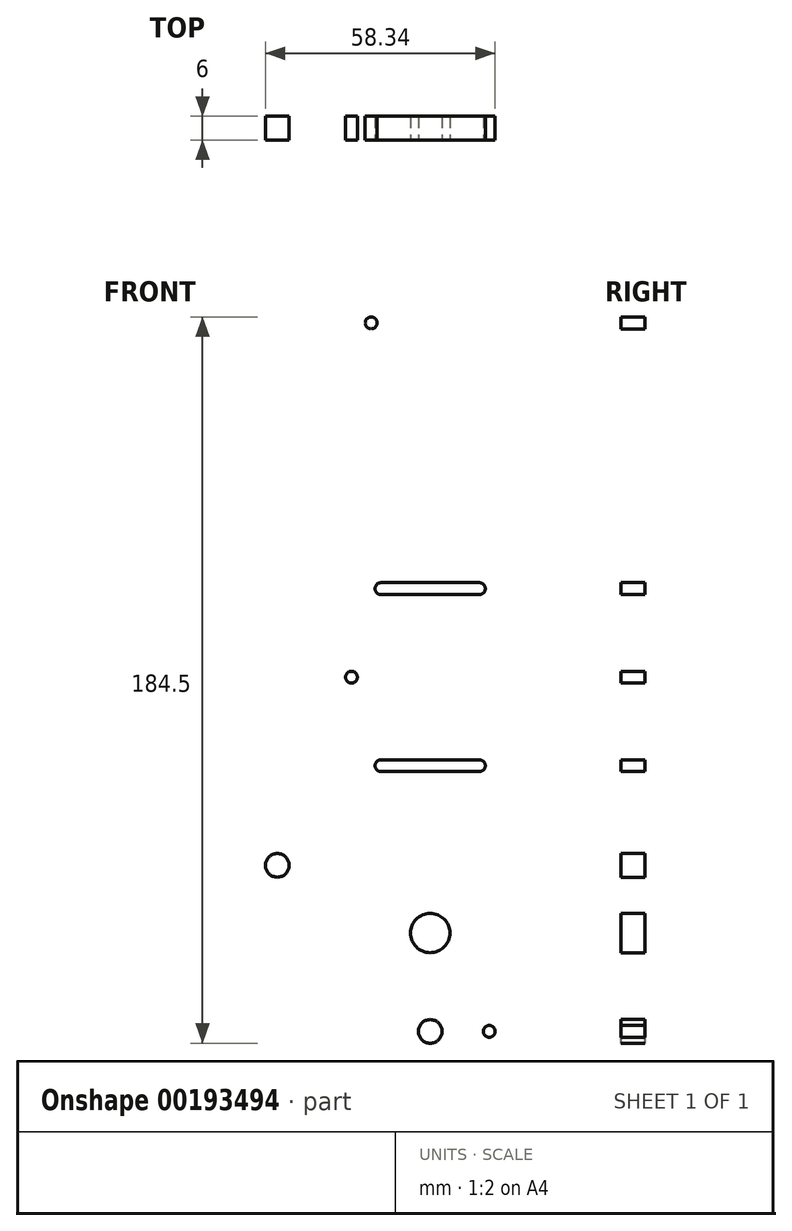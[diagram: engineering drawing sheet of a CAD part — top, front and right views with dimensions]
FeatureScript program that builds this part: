
annotation { "Feature Type Name" : "Feature", "Feature Type Description" : "" }
export const myFeature = defineFeature(function(context is Context, id is Id, definition is map)
    precondition{}
    {
        {
            var Q0;
            Q0=qCreatedBy(makeId("Front.planeOp"),FACE);
            var sketch = newSketch(context, id + "F0", { "sketchPlane" : qUnion([Q0])});
            skLineSegment(sketch, "E0.bottom", {"start": v(-75, 100) * mm, "end": v(75, 100) * mm});
            skLineSegment(sketch, "E0.top", {"start": v(-75, -100) * mm, "end": v(75, -100) * mm});
            skLineSegment(sketch, "E0.left", {"start": v(-75, 100) * mm, "end": v(-75, -100) * mm});
            skLineSegment(sketch, "E0.right", {"start": v(75, 100) * mm, "end": v(75, -100) * mm});
            skPoint(sketch, "E0.middle", {"position": v(0, 0) * mm});
            skSolve(sketch);
        }
        {
            var Q0;
            Q0=makeQuery(id+"F0.imprint","IMPRINT",FACE,{"disambiguationData":[TD([[makeQuery(id+"F0.imprint","IMPRINT",EDGE,{"derivedFrom":sQuery(id+"F0.wireOp",EDGE,"E0.bottom")}),-1.0]])]});
            extrude(context, id + "F1", {"entities" : qUnion([Q0]), "depth" : 3 * mm, "hasSecondDirection" : true, "secondDirectionOppositeDirection" : true, "secondDirectionDepth" : 3 * mm});
        }
        {
            var Q0;
            Q0=makeQuery(id+"F1.opExtrude","SWEPT_EDGE",EDGE,{"disambiguationData":[OSD([sQuery(id+"F0.wireOp",EDGE,"E0.top"),sQuery(id+"F0.wireOp",EDGE,"E0.left")])]});
            var Q1;
            Q1=makeQuery(id+"F1.opExtrude","SWEPT_EDGE",EDGE,{"disambiguationData":[OSD([sQuery(id+"F0.wireOp",EDGE,"E0.top"),sQuery(id+"F0.wireOp",EDGE,"E0.right")])]});
            var Q2;
            Q2=makeQuery(id+"F1.opExtrude","SWEPT_EDGE",EDGE,{"disambiguationData":[OSD([sQuery(id+"F0.wireOp",EDGE,"E0.bottom"),sQuery(id+"F0.wireOp",EDGE,"E0.right")])]});
            var Q3;
            Q3=makeQuery(id+"F1.opExtrude","SWEPT_EDGE",EDGE,{"disambiguationData":[OSD([sQuery(id+"F0.wireOp",EDGE,"E0.bottom"),sQuery(id+"F0.wireOp",EDGE,"E0.left")])]});
            fillet(context, id + "F2", {"entities" : qUnion([Q0, Q1, Q2, Q3]), "radius" : 10 * mm, "tangentPropagation" : true, "allowEdgeOverflow" : false});
        }
        {
            var Q0;
            Q0=makeQuery(id+"F1.opExtrude","CAP_FACE",FACE,{"disambiguationData":[OSD([sQuery(id+"F0.wireOp",EDGE,"E0.bottom"),sQuery(id+"F0.wireOp",EDGE,"E0.top"),sQuery(id+"F0.wireOp",EDGE,"E0.left"),sQuery(id+"F0.wireOp",EDGE,"E0.right")])],"isStart":false});
            var sketch = newSketch(context, id + "F3", { "sketchPlane" : qUnion([Q0])});
            skPoint(sketch, "E1.middle", {"position": v(0, 0) * mm});
            skPoint(sketch, "E2", {"position": v(62.5, -80) * mm});
            skPoint(sketch, "E3", {"position": v(62.5, -50) * mm});
            skPoint(sketch, "E4.MirrorP", {"position": v(-62.5, -50) * mm});
            skPoint(sketch, "E5.MirrorP", {"position": v(-62.5, -80) * mm});
            skPoint(sketch, "E6.MirrorP", {"position": v(62.5, 50) * mm});
            skPoint(sketch, "E7.MirrorP", {"position": v(62.5, 80) * mm});
            skPoint(sketch, "E8.MirrorP", {"position": v(-62.5, 50) * mm});
            skPoint(sketch, "E9.MirrorP", {"position": v(-62.5, 80) * mm});
            skSolve(sketch);
        }
        {
            var Q0;
            Q0=sQuery(id+"F3.wireOp",VERTEX,"E2");
            var Q1;
            Q1=sQuery(id+"F3.wireOp",VERTEX,"E3");
            var Q2;
            Q2=sQuery(id+"F3.wireOp",VERTEX,"E6.MirrorP");
            var Q3;
            Q3=sQuery(id+"F3.wireOp",VERTEX,"E7.MirrorP");
            var Q4;
            Q4=sQuery(id+"F3.wireOp",VERTEX,"E9.MirrorP");
            var Q5;
            Q5=sQuery(id+"F3.wireOp",VERTEX,"E8.MirrorP");
            var Q6;
            Q6=sQuery(id+"F3.wireOp",VERTEX,"E4.MirrorP");
            var Q7;
            Q7=sQuery(id+"F3.wireOp",VERTEX,"E5.MirrorP");
            var Q8;
            Q8=makeQuery(id+"F1.opExtrude","SWEPT_BODY",BODY,{"disambiguationData":[OSD([sQuery(id+"F0.wireOp",EDGE,"E0.bottom"),sQuery(id+"F0.wireOp",EDGE,"E0.top"),sQuery(id+"F0.wireOp",EDGE,"E0.left"),sQuery(id+"F0.wireOp",EDGE,"E0.right")])]});
            hole(context, id + "F4", {"style" : HoleStyle.SIMPLE, "endStyle" : HoleEndStyle.BLIND, "holeDiameter" : 3 * mm, "holeDepth" : 12 * mm, "locations" : qUnion([Q0, Q1, Q2, Q3, Q4, Q5, Q6, Q7]), "scope" : qUnion([Q8])});
        }
        {
            var Q0;
            Q0=makeQuery(id+"F1.opExtrude","CAP_FACE",FACE,{"disambiguationData":[OSD([sQuery(id+"F0.wireOp",EDGE,"E0.bottom"),sQuery(id+"F0.wireOp",EDGE,"E0.top"),sQuery(id+"F0.wireOp",EDGE,"E0.left"),sQuery(id+"F0.wireOp",EDGE,"E0.right")])],"isStart":false});
            var sketch = newSketch(context, id + "F5", { "sketchPlane" : qUnion([Q0])});
            skPoint(sketch, "E10.middle", {"position": v(0, 0) * mm});
            skLineSegment(sketch, "E11.bottom", {"start": v(48, 10) * mm, "end": v(32, 10) * mm});
            skLineSegment(sketch, "E11.top", {"start": v(48, -10) * mm, "end": v(32, -10) * mm});
            skLineSegment(sketch, "E11.left", {"start": v(48, 10) * mm, "end": v(48, -10) * mm});
            skLineSegment(sketch, "E11.right", {"start": v(32, 10) * mm, "end": v(32, -10) * mm});
            skPoint(sketch, "E11.middle", {"position": v(40, 0) * mm});
            skPoint(sketch, "E12.MirrorP", {"position": v(-40, 0) * mm});
            skLineSegment(sketch, "E13.MirrorCS", {"start": v(-48, 10) * mm, "end": v(-32, 10) * mm});
            skLineSegment(sketch, "E14.MirrorCS", {"start": v(-32, 10) * mm, "end": v(-32, -10) * mm});
            skLineSegment(sketch, "E15.MirrorCS", {"start": v(-48, -10) * mm, "end": v(-32, -10) * mm});
            skLineSegment(sketch, "E16.MirrorCS", {"start": v(-48, 10) * mm, "end": v(-48, -10) * mm});
            skArc(sketch, "E17.0.startCap", {"start": v(12.5, 24) * mm, "mid": v(14, 22.5) * mm, "end": v(12.5, 21) * mm});
            skArc(sketch, "E17.0.endCap", {"start": v(-12.5, 21) * mm, "mid": v(-14, 22.5) * mm, "end": v(-12.5, 24) * mm});
            skLineSegment(sketch, "E17.0.left", {"start": v(12.5, 21) * mm, "end": v(-12.5, 21) * mm});
            skLineSegment(sketch, "E17.0.right", {"start": v(12.5, 24) * mm, "end": v(-12.5, 24) * mm});
            skArc(sketch, "E18.0.startCap", {"start": v(12.5, -21) * mm, "mid": v(14, -22.5) * mm, "end": v(12.5, -24) * mm});
            skArc(sketch, "E18.0.endCap", {"start": v(-12.5, -24) * mm, "mid": v(-14, -22.5) * mm, "end": v(-12.5, -21) * mm});
            skLineSegment(sketch, "E18.0.left", {"start": v(12.5, -24) * mm, "end": v(-12.5, -24) * mm});
            skLineSegment(sketch, "E18.0.right", {"start": v(12.5, -21) * mm, "end": v(-12.5, -21) * mm});
            skCircle(sketch, "E19", {"center": v(0, 65) * mm, "radius": 5 * mm});
            skCircle(sketch, "E20.MirrorC", {"center": v(0, -65) * mm, "radius": 5 * mm});
            skPoint(sketch, "E21.endSnap0", {"position": v(0, 100) * mm});
            skCircle(sketch, "E22", {"center": v(0, 90) * mm, "radius": 3 * mm});
            skCircle(sketch, "E23", {"center": v(15, 90) * mm, "radius": 1.5 * mm});
            skCircle(sketch, "E24.MirrorC", {"center": v(-15, 90) * mm, "radius": 1.5 * mm});
            skCircle(sketch, "E25.MirrorC", {"center": v(-15, -90) * mm, "radius": 1.5 * mm});
            skCircle(sketch, "E26.MirrorC", {"center": v(15, -90) * mm, "radius": 1.5 * mm});
            skCircle(sketch, "E27.MirrorC", {"center": v(0, -90) * mm, "radius": 3 * mm});
            skCircle(sketch, "E28", {"center": v(20, 0) * mm, "radius": 1.5 * mm});
            skCircle(sketch, "E29.MirrorC", {"center": v(-20, 0) * mm, "radius": 1.5 * mm});
            skCircle(sketch, "E30", {"center": v(38.84, -47.82) * mm, "radius": 3 * mm});
            skCircle(sketch, "E31.MirrorC", {"center": v(-38.84, -47.82) * mm, "radius": 3 * mm});
            skSolve(sketch);
        }
        {
            var Q0;
            Q0=makeQuery(id+"F5.imprint","IMPRINT",FACE,{"disambiguationData":[TD([[makeQuery(id+"F5.imprint","IMPRINT",EDGE,{"derivedFrom":sQuery(id+"F5.wireOp",EDGE,"E13.MirrorCS")}),-1.0]])]});
            var Q1;
            Q1=makeQuery(id+"F5.imprint","IMPRINT",FACE,{"disambiguationData":[TD([[makeQuery(id+"F5.imprint","IMPRINT",EDGE,{"derivedFrom":sQuery(id+"F5.wireOp",EDGE,"E17.0.startCap")}),-1.0]])]});
            var Q2;
            Q2=makeQuery(id+"F5.imprint","IMPRINT",FACE,{"disambiguationData":[TD([[makeQuery(id+"F5.imprint","IMPRINT",EDGE,{"derivedFrom":sQuery(id+"F5.wireOp",EDGE,"E18.0.startCap")}),-1.0]])]});
            var Q3;
            Q3=makeQuery(id+"F5.imprint","IMPRINT",FACE,{"disambiguationData":[TD([[makeQuery(id+"F5.imprint","IMPRINT",EDGE,{"derivedFrom":sQuery(id+"F5.wireOp",EDGE,"E11.bottom")}),1.0]])]});
            var Q4;
            Q4=makeQuery(id+"F5.imprint","IMPRINT",FACE,{"disambiguationData":[TD([[makeQuery(id+"F5.imprint","IMPRINT",EDGE,{"derivedFrom":sQuery(id+"F5.wireOp",EDGE,"E28")}),1.0]])]});
            var Q5;
            Q5=makeQuery(id+"F5.imprint","IMPRINT",FACE,{"disambiguationData":[TD([[makeQuery(id+"F5.imprint","IMPRINT",EDGE,{"derivedFrom":sQuery(id+"F5.wireOp",EDGE,"E20.MirrorC")}),-1.0]])]});
            var Q6;
            Q6=makeQuery(id+"F5.imprint","IMPRINT",FACE,{"disambiguationData":[TD([[makeQuery(id+"F5.imprint","IMPRINT",EDGE,{"derivedFrom":sQuery(id+"F5.wireOp",EDGE,"E31.MirrorC")}),-1.0]])]});
            var Q7;
            Q7=makeQuery(id+"F5.imprint","IMPRINT",FACE,{"disambiguationData":[TD([[makeQuery(id+"F5.imprint","IMPRINT",EDGE,{"derivedFrom":sQuery(id+"F5.wireOp",EDGE,"E30")}),1.0]])]});
            var Q8;
            Q8=makeQuery(id+"F5.imprint","IMPRINT",FACE,{"disambiguationData":[TD([[makeQuery(id+"F5.imprint","IMPRINT",EDGE,{"derivedFrom":sQuery(id+"F5.wireOp",EDGE,"E27.MirrorC")}),-1.0]])]});
            var Q9;
            Q9=makeQuery(id+"F5.imprint","IMPRINT",FACE,{"disambiguationData":[TD([[makeQuery(id+"F5.imprint","IMPRINT",EDGE,{"derivedFrom":sQuery(id+"F5.wireOp",EDGE,"E29.MirrorC")}),-1.0]])]});
            var Q10;
            Q10=makeQuery(id+"F5.imprint","IMPRINT",FACE,{"disambiguationData":[TD([[makeQuery(id+"F5.imprint","IMPRINT",EDGE,{"derivedFrom":sQuery(id+"F5.wireOp",EDGE,"E26.MirrorC")}),-1.0]])]});
            var Q11;
            Q11=makeQuery(id+"F5.imprint","IMPRINT",FACE,{"disambiguationData":[TD([[makeQuery(id+"F5.imprint","IMPRINT",EDGE,{"derivedFrom":sQuery(id+"F5.wireOp",EDGE,"E25.MirrorC")}),1.0]])]});
            var Q12;
            Q12=makeQuery(id+"F5.imprint","IMPRINT",FACE,{"disambiguationData":[TD([[makeQuery(id+"F5.imprint","IMPRINT",EDGE,{"derivedFrom":sQuery(id+"F5.wireOp",EDGE,"E19")}),1.0]])]});
            var Q13;
            Q13=makeQuery(id+"F5.imprint","IMPRINT",FACE,{"disambiguationData":[TD([[makeQuery(id+"F5.imprint","IMPRINT",EDGE,{"derivedFrom":sQuery(id+"F5.wireOp",EDGE,"E22")}),1.0]])]});
            var Q14;
            Q14=makeQuery(id+"F5.imprint","IMPRINT",FACE,{"disambiguationData":[TD([[makeQuery(id+"F5.imprint","IMPRINT",EDGE,{"derivedFrom":sQuery(id+"F5.wireOp",EDGE,"E24.MirrorC")}),-1.0]])]});
            var Q15;
            Q15=makeQuery(id+"F5.imprint","IMPRINT",FACE,{"disambiguationData":[TD([[makeQuery(id+"F5.imprint","IMPRINT",EDGE,{"derivedFrom":sQuery(id+"F5.wireOp",EDGE,"E23")}),1.0]])]});
            extrude(context, id + "F6", {"entities" : qUnion([Q0, Q1, Q2, Q3, Q4, Q5, Q6, Q7, Q8, Q9, Q10, Q11, Q12, Q13, Q14, Q15]), "operationType" : NewBodyOperationType.REMOVE, "oppositeDirection" : true, "depth" : 25 * mm});
        }
    });
